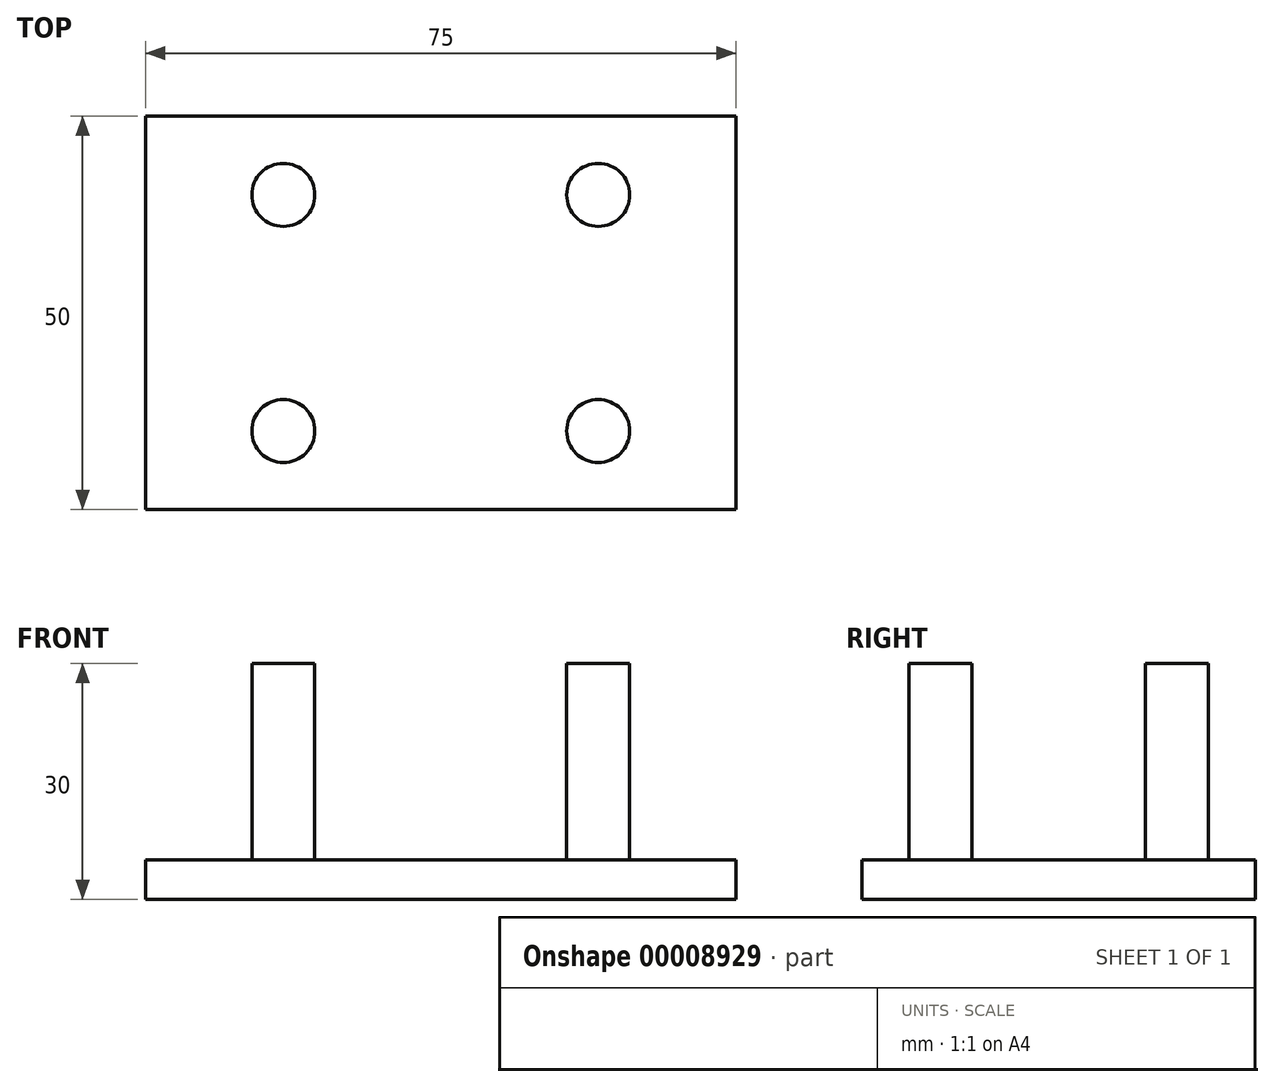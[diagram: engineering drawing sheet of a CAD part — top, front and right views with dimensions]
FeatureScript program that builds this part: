
annotation { "Feature Type Name" : "Feature", "Feature Type Description" : "" }
export const myFeature = defineFeature(function(context is Context, id is Id, definition is map)
    precondition{}
    {
        {
            var Q0;
            Q0=qCreatedBy(makeId("Top.planeOp"),FACE);
            var sketch = newSketch(context, id + "F0", { "sketchPlane" : qUnion([Q0])});
            skLineSegment(sketch, "E0.rect.bottom", {"start": v(37.5, 25) * mm, "end": v(-37.5, 25) * mm});
            skLineSegment(sketch, "E0.rect.top", {"start": v(37.5, -25) * mm, "end": v(-37.5, -25) * mm});
            skLineSegment(sketch, "E0.rect.left", {"start": v(37.5, 25) * mm, "end": v(37.5, -25) * mm});
            skLineSegment(sketch, "E0.rect.right", {"start": v(-37.5, 25) * mm, "end": v(-37.5, -25) * mm});
            skPoint(sketch, "E0.rect.middle", {"position": v(0, 0) * mm});
            skSolve(sketch);
        }
        {
            var Q0;
            Q0 = qSketchRegion(id + "F0", true);
            extrude(context, id + "F1", {"entities" : qUnion([Q0]), "depth" : 5 * mm});
        }
        {
            var Q0;
            Q0=makeQuery(id+"F1.opExtrude","CAP_FACE",FACE,{"disambiguationData":[OSD([sQuery(id+"F0.wireOp",EDGE,"E0.rect.bottom"),sQuery(id+"F0.wireOp",EDGE,"E0.rect.top"),sQuery(id+"F0.wireOp",EDGE,"E0.rect.left"),sQuery(id+"F0.wireOp",EDGE,"E0.rect.right")])],"isStart":false});
            var sketch = newSketch(context, id + "F2", { "sketchPlane" : qUnion([Q0])});
            skLineSegment(sketch, "E1", {"start": v(16, 15) * mm, "end": v(20, 15) * mm});
            skLineSegment(sketch, "E2", {"start": v(20, 15) * mm, "end": v(20, 11) * mm});
            skLineSegment(sketch, "E3.0.MirrorCS", {"start": v(16, -15) * mm, "end": v(20, -15) * mm});
            skLineSegment(sketch, "E4.0.MirrorCS", {"start": v(20, -15) * mm, "end": v(20, -11) * mm});
            skCircle(sketch, "E5", {"center": v(-20, 15) * mm, "radius": 4 * mm});
            skCircle(sketch, "E6.0.MirrorC", {"center": v(20, 15) * mm, "radius": 4 * mm});
            skCircle(sketch, "E7.0.MirrorC", {"center": v(-20, -15) * mm, "radius": 4 * mm});
            skCircle(sketch, "E8.0.MirrorC", {"center": v(20, -15) * mm, "radius": 4 * mm});
            skPoint(sketch, "E9.orphan", {"position": v(0, 15) * mm});
            skPoint(sketch, "E10.orphan", {"position": v(-20, 0) * mm});
            skPoint(sketch, "E11.trimOffspring.end.orphan", {"position": v(0, -25) * mm});
            skPoint(sketch, "E12.start.orphan", {"position": v(0, 25) * mm});
            skPoint(sketch, "E13.0.MirrorCS.start.orphan", {"position": v(37.5, 0) * mm});
            skPoint(sketch, "E14.end.orphan", {"position": v(-37.5, 0) * mm});
            skSolve(sketch);
        }
        {
            var Q0;
            Q0 = qSketchRegion(id + "F2", true);
            extrude(context, id + "F3", {"entities" : qUnion([Q0]), "operationType" : NewBodyOperationType.ADD, "depth" : 25 * mm});
        }
    });
